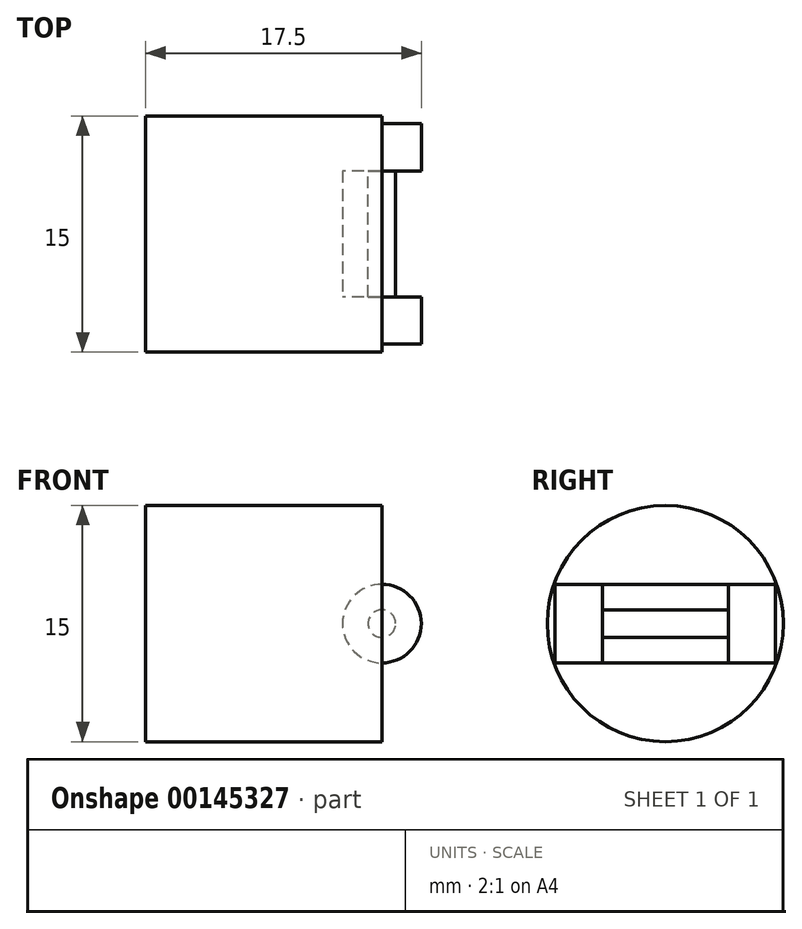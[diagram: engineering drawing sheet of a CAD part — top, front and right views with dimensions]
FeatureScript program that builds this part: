
annotation { "Feature Type Name" : "Feature", "Feature Type Description" : "" }
export const myFeature = defineFeature(function(context is Context, id is Id, definition is map)
    precondition{}
    {
        {
            var Q0;
            Q0=qCreatedBy(makeId("Right.planeOp"),FACE);
            var sketch = newSketch(context, id + "F0", { "sketchPlane" : qUnion([Q0])});
            skCircle(sketch, "E0", {"center": v(0, 0) * mm, "radius": 7.5 * mm});
            skSolve(sketch);
        }
        {
            var Q0;
            Q0 = qSketchRegion(id + "F0", true);
            extrude(context, id + "F1", {"entities" : qUnion([Q0]), "endBound" : BoundingType.SYMMETRIC, "depth" : 15 * mm});
        }
        {
            var Q0;
            Q0=qCreatedBy(makeId("Front.planeOp"),FACE);
            var sketch = newSketch(context, id + "F2", { "sketchPlane" : qUnion([Q0])});
            skCircle(sketch, "E1", {"center": v(7.5, 0) * mm, "radius": 2.5 * mm});
            skSolve(sketch);
        }
        {
            var Q0;
            Q0 = qSketchRegion(id + "F2", true);
            extrude(context, id + "F3", {"entities" : qUnion([Q0]), "operationType" : NewBodyOperationType.ADD, "endBound" : BoundingType.SYMMETRIC, "depth" : 14 * mm});
        }
        {
            var Q0;
            Q0=qCreatedBy(makeId("Front.planeOp"),FACE);
            var sketch = newSketch(context, id + "F4", { "sketchPlane" : qUnion([Q0])});
            skCircle(sketch, "E2", {"center": v(7.5, 0) * mm, "radius": 2.5 * mm});
            skSolve(sketch);
        }
        {
            var Q0;
            Q0 = qSketchRegion(id + "F4", true);
            extrude(context, id + "F5", {"entities" : qUnion([Q0]), "operationType" : NewBodyOperationType.REMOVE, "endBound" : BoundingType.SYMMETRIC, "oppositeDirection" : true, "depth" : 8 * mm});
        }
        {
            var Q0;
            Q0=qCreatedBy(makeId("Front.planeOp"),FACE);
            var sketch = newSketch(context, id + "F6", { "sketchPlane" : qUnion([Q0])});
            skCircle(sketch, "E3", {"center": v(7.5, 0) * mm, "radius": 0.88 * mm});
            skSolve(sketch);
        }
        {
            var Q0;
            Q0 = qSketchRegion(id + "F6", true);
            extrude(context, id + "F7", {"entities" : qUnion([Q0]), "operationType" : NewBodyOperationType.ADD, "endBound" : BoundingType.SYMMETRIC, "depth" : 8 * mm});
        }
    });
